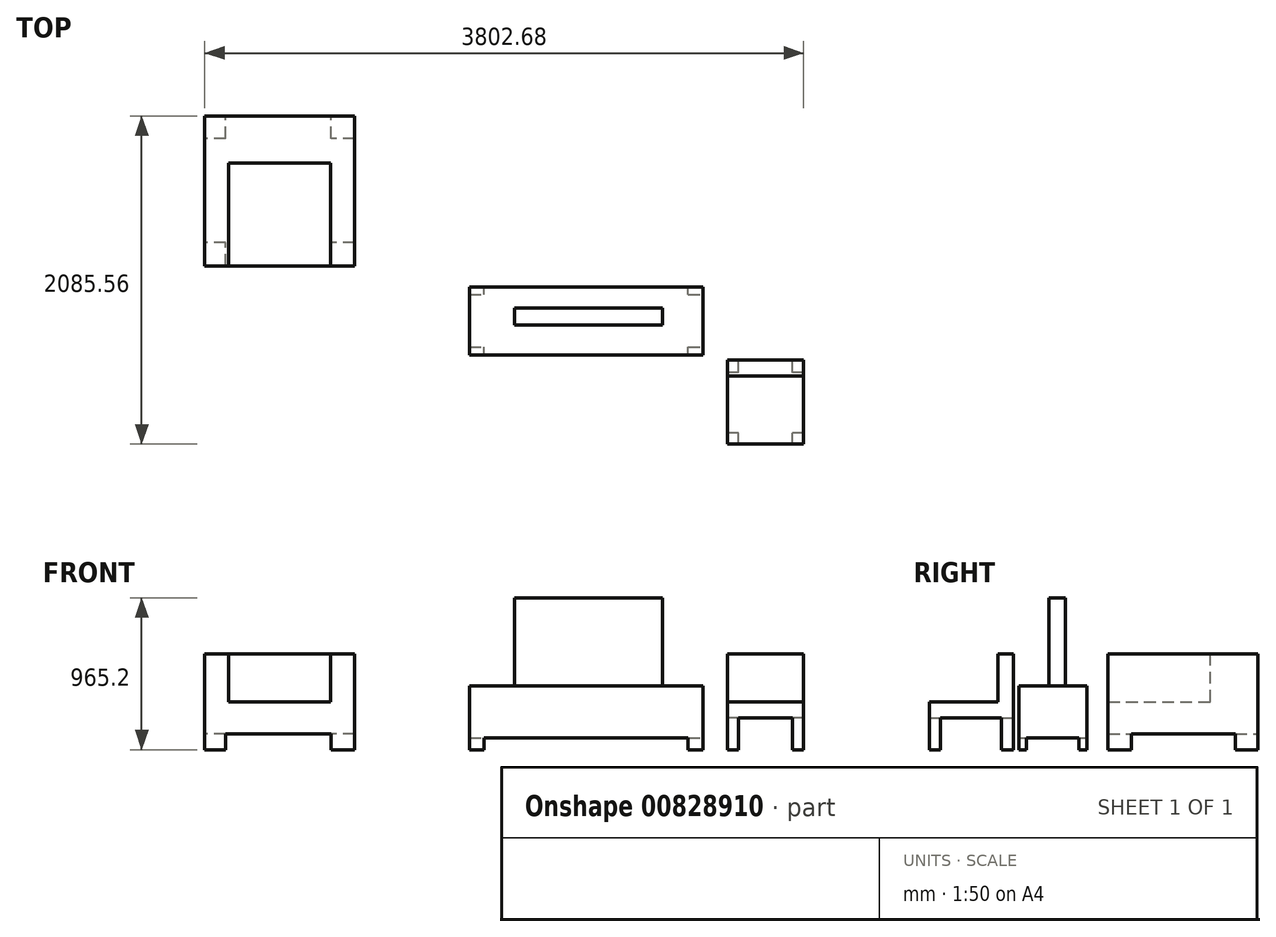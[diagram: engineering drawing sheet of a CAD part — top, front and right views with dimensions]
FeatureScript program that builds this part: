
annotation { "Feature Type Name" : "Feature", "Feature Type Description" : "" }
export const myFeature = defineFeature(function(context is Context, id is Id, definition is map)
    precondition{}
    {
        {
            var Q0;
            Q0=qCreatedBy(makeId("Top.planeOp"),FACE);
            var sketch = newSketch(context, id + "F0", { "sketchPlane" : qUnion([Q0])});
            skLineSegment(sketch, "E0.bottom", {"start": v(741.36, -215.9) * mm, "end": v(-741.36, -215.9) * mm});
            skLineSegment(sketch, "E0.top", {"start": v(741.36, 215.9) * mm, "end": v(-741.36, 215.9) * mm});
            skLineSegment(sketch, "E0.left", {"start": v(741.36, -215.9) * mm, "end": v(741.36, 215.9) * mm});
            skLineSegment(sketch, "E0.right", {"start": v(-741.36, -215.9) * mm, "end": v(-741.36, 215.9) * mm});
            skPoint(sketch, "E0.middle", {"position": v(0, 0) * mm});
            skSolve(sketch);
        }
        {
            var Q0;
            Q0 = qSketchRegion(id + "F0", true);
            extrude(context, id + "F1", {"entities" : qUnion([Q0]), "depth" : 406.4 * mm, "offsetDistance" : 25.4 * mm});
        }
        {
            var Q0;
            Q0=makeQuery(id+"F1.opExtrude","CAP_FACE",FACE,{"disambiguationData":[OSD([sQuery(id+"F0.wireOp",EDGE,"E0.bottom"),sQuery(id+"F0.wireOp",EDGE,"E0.top"),sQuery(id+"F0.wireOp",EDGE,"E0.left"),sQuery(id+"F0.wireOp",EDGE,"E0.right")])],"isStart":true});
            var sketch = newSketch(context, id + "F2", { "sketchPlane" : qUnion([Q0])});
            skLineSegment(sketch, "E1.bottom", {"start": v(647.65, 215.9) * mm, "end": v(-647.65, 215.9) * mm});
            skLineSegment(sketch, "E1.top", {"start": v(647.65, -215.9) * mm, "end": v(-647.65, -215.9) * mm});
            skLineSegment(sketch, "E1.left", {"start": v(647.65, 215.9) * mm, "end": v(647.65, 166.65) * mm});
            skLineSegment(sketch, "E1.right", {"start": v(-647.65, 215.9) * mm, "end": v(-647.65, 166.65) * mm});
            skPoint(sketch, "E1.middle", {"position": v(0, 0) * mm});
            skLineSegment(sketch, "E2.bottom", {"start": v(-741.36, -166.65) * mm, "end": v(-647.65, -166.65) * mm});
            skLineSegment(sketch, "E2.top", {"start": v(-741.36, 166.65) * mm, "end": v(-647.65, 166.65) * mm});
            skLineSegment(sketch, "E2.left", {"start": v(-741.36, -166.65) * mm, "end": v(-741.36, 166.65) * mm});
            skLineSegment(sketch, "E2.right", {"start": v(741.36, -166.65) * mm, "end": v(741.36, 166.65) * mm});
            skLineSegment(sketch, "E3.trimOffspring", {"start": v(-647.65, -166.65) * mm, "end": v(-647.65, -215.9) * mm});
            skLineSegment(sketch, "E4.trimOffspring", {"start": v(647.65, 166.65) * mm, "end": v(741.36, 166.65) * mm});
            skLineSegment(sketch, "E5.trimOffspring", {"start": v(647.65, -166.65) * mm, "end": v(647.65, -215.9) * mm});
            skLineSegment(sketch, "E6.trimOffspring", {"start": v(647.65, -166.65) * mm, "end": v(741.36, -166.65) * mm});
            skSolve(sketch);
        }
        {
            var Q0;
            Q0 = qSketchRegion(id + "F2", true);
            extrude(context, id + "F3", {"entities" : qUnion([Q0]), "operationType" : NewBodyOperationType.REMOVE, "oppositeDirection" : true, "depth" : 76.2 * mm, "offsetDistance" : 25.4 * mm});
        }
        {
            var Q0;
            Q0=qCreatedBy(makeId("Top.planeOp"),FACE);
            var sketch = newSketch(context, id + "F4", { "sketchPlane" : qUnion([Q0])});
            skLineSegment(sketch, "E7.bottom", {"start": v(1381.43, -783.45) * mm, "end": v(898.83, -783.45) * mm});
            skLineSegment(sketch, "E7.top", {"start": v(1381.43, -250.05) * mm, "end": v(898.83, -250.05) * mm});
            skLineSegment(sketch, "E7.left", {"start": v(1381.43, -783.45) * mm, "end": v(1381.43, -250.05) * mm});
            skLineSegment(sketch, "E7.right", {"start": v(898.83, -783.45) * mm, "end": v(898.83, -250.05) * mm});
            skPoint(sketch, "E7.middle", {"position": v(1140.13, -516.75) * mm});
            skSolve(sketch);
        }
        {
            var Q0;
            Q0 = qSketchRegion(id + "F4", true);
            extrude(context, id + "F5", {"entities" : qUnion([Q0]), "depth" : 609.6 * mm, "offsetDistance" : 25.4 * mm});
        }
        {
            var Q0;
            Q0=makeQuery(id+"F5.opExtrude","CAP_FACE",FACE,{"disambiguationData":[OSD([sQuery(id+"F4.wireOp",EDGE,"E7.bottom"),sQuery(id+"F4.wireOp",EDGE,"E7.top"),sQuery(id+"F4.wireOp",EDGE,"E7.left"),sQuery(id+"F4.wireOp",EDGE,"E7.right")])],"isStart":true});
            var sketch = newSketch(context, id + "F6", { "sketchPlane" : qUnion([Q0])});
            skLineSegment(sketch, "E8.bottom", {"start": v(969.42, 783.45) * mm, "end": v(1310.85, 783.45) * mm});
            skLineSegment(sketch, "E8.top", {"start": v(969.42, 250.05) * mm, "end": v(1310.85, 250.05) * mm});
            skLineSegment(sketch, "E8.left", {"start": v(969.42, 783.45) * mm, "end": v(969.42, 713.3) * mm});
            skLineSegment(sketch, "E8.right", {"start": v(1310.85, 783.45) * mm, "end": v(1310.85, 713.3) * mm});
            skLineSegment(sketch, "E9.bottom", {"start": v(1381.43, 327.74) * mm, "end": v(1310.85, 327.74) * mm});
            skLineSegment(sketch, "E9.top", {"start": v(1381.43, 713.3) * mm, "end": v(1310.85, 713.3) * mm});
            skLineSegment(sketch, "E9.left", {"start": v(1381.43, 327.74) * mm, "end": v(1381.43, 713.3) * mm});
            skLineSegment(sketch, "E9.right", {"start": v(898.83, 327.74) * mm, "end": v(898.83, 713.3) * mm});
            skLineSegment(sketch, "E10.trimOffspring", {"start": v(969.42, 713.3) * mm, "end": v(898.83, 713.3) * mm});
            skLineSegment(sketch, "E11.trimOffspring", {"start": v(969.42, 327.74) * mm, "end": v(969.42, 250.05) * mm});
            skLineSegment(sketch, "E12.trimOffspring", {"start": v(1310.85, 327.74) * mm, "end": v(1310.85, 250.05) * mm});
            skLineSegment(sketch, "E13.trimOffspring", {"start": v(969.42, 327.74) * mm, "end": v(898.83, 327.74) * mm});
            skSolve(sketch);
        }
        {
            var Q0;
            Q0 = qSketchRegion(id + "F6", true);
            extrude(context, id + "F7", {"entities" : qUnion([Q0]), "operationType" : NewBodyOperationType.REMOVE, "oppositeDirection" : true, "depth" : 203.2 * mm, "offsetDistance" : 25.4 * mm});
        }
        {
            var Q0;
            Q0=makeQuery(id+"F5.opExtrude","CAP_FACE",FACE,{"disambiguationData":[OSD([sQuery(id+"F4.wireOp",EDGE,"E7.bottom"),sQuery(id+"F4.wireOp",EDGE,"E7.top"),sQuery(id+"F4.wireOp",EDGE,"E7.left"),sQuery(id+"F4.wireOp",EDGE,"E7.right")])],"isStart":false});
            var sketch = newSketch(context, id + "F8", { "sketchPlane" : qUnion([Q0])});
            skLineSegment(sketch, "E14.bottom", {"start": v(1381.43, -349.66) * mm, "end": v(898.83, -349.66) * mm});
            skLineSegment(sketch, "E14.top", {"start": v(1381.43, -783.45) * mm, "end": v(898.83, -783.45) * mm});
            skLineSegment(sketch, "E14.left", {"start": v(1381.43, -349.66) * mm, "end": v(1381.43, -783.45) * mm});
            skLineSegment(sketch, "E14.right", {"start": v(898.83, -349.66) * mm, "end": v(898.83, -783.45) * mm});
            skSolve(sketch);
        }
        {
            var Q0;
            Q0 = qSketchRegion(id + "F8", true);
            extrude(context, id + "F9", {"entities" : qUnion([Q0]), "operationType" : NewBodyOperationType.REMOVE, "oppositeDirection" : true, "depth" : 304.8 * mm, "offsetDistance" : 25.4 * mm});
        }
        {
            var Q0;
            Q0=makeQuery(id+"F1.opExtrude","CAP_FACE",FACE,{"disambiguationData":[OSD([sQuery(id+"F0.wireOp",EDGE,"E0.bottom"),sQuery(id+"F0.wireOp",EDGE,"E0.top"),sQuery(id+"F0.wireOp",EDGE,"E0.left"),sQuery(id+"F0.wireOp",EDGE,"E0.right")])],"isStart":false});
            var sketch = newSketch(context, id + "F10", { "sketchPlane" : qUnion([Q0])});
            skLineSegment(sketch, "E15.bottom", {"start": v(-454.65, -25.24) * mm, "end": v(485.15, -25.24) * mm});
            skLineSegment(sketch, "E15.top", {"start": v(-454.65, 81.56) * mm, "end": v(485.15, 81.56) * mm});
            skLineSegment(sketch, "E15.left", {"start": v(-454.65, -25.24) * mm, "end": v(-454.65, 81.56) * mm});
            skLineSegment(sketch, "E15.right", {"start": v(485.15, -25.24) * mm, "end": v(485.15, 81.56) * mm});
            skSolve(sketch);
        }
        {
            var Q0;
            Q0 = qSketchRegion(id + "F10", true);
            extrude(context, id + "F11", {"entities" : qUnion([Q0]), "operationType" : NewBodyOperationType.ADD, "depth" : 558.8 * mm, "offsetDistance" : 25.4 * mm});
        }
        {
            var Q0;
            Q0=qCreatedBy(makeId("Top.planeOp"),FACE);
            var sketch = newSketch(context, id + "F12", { "sketchPlane" : qUnion([Q0])});
            skLineSegment(sketch, "E16.bottom", {"start": v(-2421.25, 349.6) * mm, "end": v(-1468.75, 349.6) * mm});
            skLineSegment(sketch, "E16.top", {"start": v(-2421.25, 1302.1) * mm, "end": v(-1468.75, 1302.1) * mm});
            skLineSegment(sketch, "E16.left", {"start": v(-2421.25, 349.6) * mm, "end": v(-2421.25, 1302.1) * mm});
            skLineSegment(sketch, "E16.right", {"start": v(-1468.75, 349.6) * mm, "end": v(-1468.75, 1302.1) * mm});
            skSolve(sketch);
        }
        {
            var Q0;
            Q0 = qSketchRegion(id + "F12", true);
            extrude(context, id + "F13", {"entities" : qUnion([Q0]), "depth" : 609.6 * mm, "offsetDistance" : 25.4 * mm});
        }
        {
            var Q0;
            Q0=makeQuery(id+"F13.opExtrude","CAP_FACE",FACE,{"disambiguationData":[OSD([sQuery(id+"F12.wireOp",EDGE,"E16.bottom"),sQuery(id+"F12.wireOp",EDGE,"E16.top"),sQuery(id+"F12.wireOp",EDGE,"E16.left"),sQuery(id+"F12.wireOp",EDGE,"E16.right")])],"isStart":false});
            var sketch = newSketch(context, id + "F14", { "sketchPlane" : qUnion([Q0])});
            skLineSegment(sketch, "E17.bottom", {"start": v(-2268.85, 349.6) * mm, "end": v(-1621.15, 349.6) * mm});
            skLineSegment(sketch, "E17.top", {"start": v(-2268.85, 1000.98) * mm, "end": v(-1621.15, 1000.98) * mm});
            skLineSegment(sketch, "E17.left", {"start": v(-2268.85, 349.6) * mm, "end": v(-2268.85, 1000.98) * mm});
            skLineSegment(sketch, "E17.right", {"start": v(-1621.15, 349.6) * mm, "end": v(-1621.15, 1000.98) * mm});
            skSolve(sketch);
        }
        {
            var Q0;
            Q0 = qSketchRegion(id + "F14", true);
            extrude(context, id + "F15", {"entities" : qUnion([Q0]), "operationType" : NewBodyOperationType.REMOVE, "oppositeDirection" : true, "depth" : 304.8 * mm, "offsetDistance" : 25.4 * mm});
        }
        {
            var Q0;
            Q0=makeQuery(id+"F13.opExtrude","CAP_FACE",FACE,{"disambiguationData":[OSD([sQuery(id+"F12.wireOp",EDGE,"E16.bottom"),sQuery(id+"F12.wireOp",EDGE,"E16.top"),sQuery(id+"F12.wireOp",EDGE,"E16.left"),sQuery(id+"F12.wireOp",EDGE,"E16.right")])],"isStart":true});
            var sketch = newSketch(context, id + "F16", { "sketchPlane" : qUnion([Q0])});
            skLineSegment(sketch, "E18.bottom", {"start": v(-2288.14, -349.6) * mm, "end": v(-1619.89, -349.6) * mm});
            skLineSegment(sketch, "E18.top", {"start": v(-2288.14, -1302.1) * mm, "end": v(-1619.89, -1302.1) * mm});
            skLineSegment(sketch, "E18.left", {"start": v(-2288.14, -349.6) * mm, "end": v(-2288.14, -498.56) * mm});
            skLineSegment(sketch, "E18.right", {"start": v(-1619.89, -349.6) * mm, "end": v(-1619.89, -498.56) * mm});
            skLineSegment(sketch, "E19.bottom", {"start": v(-1468.75, -1158.87) * mm, "end": v(-1619.89, -1158.87) * mm});
            skLineSegment(sketch, "E19.top", {"start": v(-1468.75, -498.56) * mm, "end": v(-1619.89, -498.56) * mm});
            skLineSegment(sketch, "E19.left", {"start": v(-1468.75, -1158.87) * mm, "end": v(-1468.75, -498.56) * mm});
            skLineSegment(sketch, "E19.right", {"start": v(-2421.25, -1158.87) * mm, "end": v(-2421.25, -498.56) * mm});
            skLineSegment(sketch, "E20.trimOffspring", {"start": v(-2288.14, -498.56) * mm, "end": v(-2421.25, -498.56) * mm});
            skLineSegment(sketch, "E21.trimOffspring", {"start": v(-2288.14, -1158.87) * mm, "end": v(-2288.14, -1302.1) * mm});
            skLineSegment(sketch, "E22.trimOffspring", {"start": v(-1619.89, -1158.87) * mm, "end": v(-1619.89, -1302.1) * mm});
            skLineSegment(sketch, "E23.trimOffspring", {"start": v(-2288.14, -1158.87) * mm, "end": v(-2421.25, -1158.87) * mm});
            skSolve(sketch);
        }
        {
            var Q0;
            Q0 = qSketchRegion(id + "F16", true);
            extrude(context, id + "F17", {"entities" : qUnion([Q0]), "operationType" : NewBodyOperationType.REMOVE, "oppositeDirection" : true, "depth" : 101.6 * mm, "offsetDistance" : 25.4 * mm});
        }
    });
